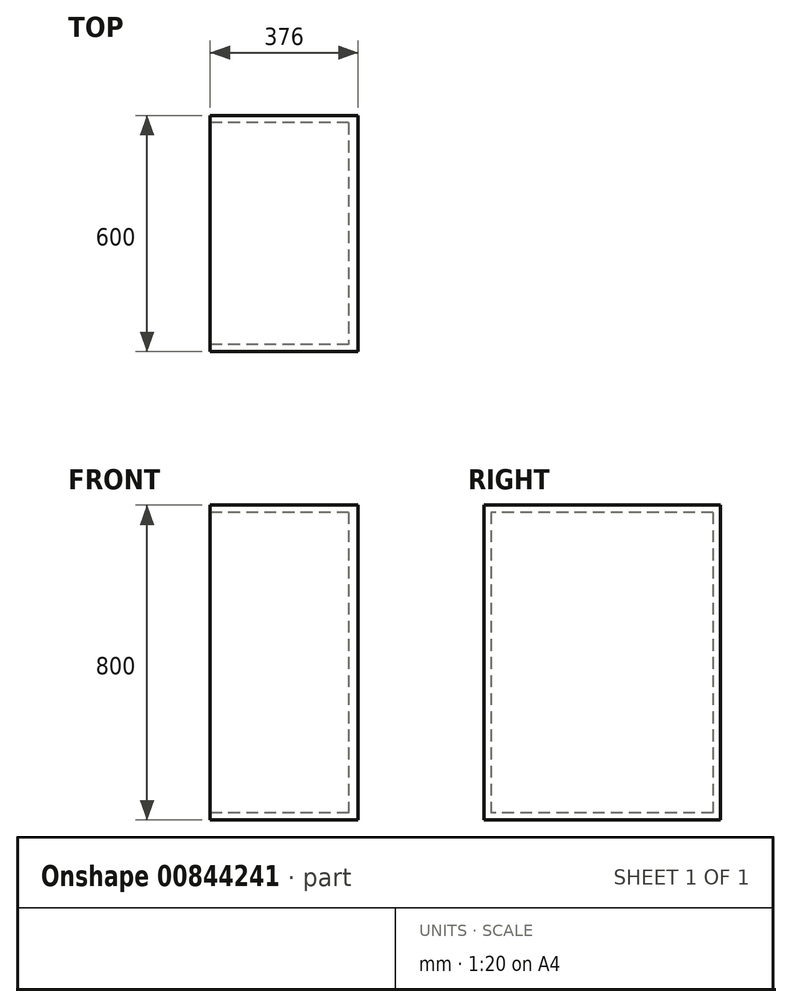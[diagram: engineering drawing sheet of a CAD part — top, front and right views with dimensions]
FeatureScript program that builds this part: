
annotation { "Feature Type Name" : "Feature", "Feature Type Description" : "" }
export const myFeature = defineFeature(function(context is Context, id is Id, definition is map)
    precondition{}
    {
        {
            var Q0;
            Q0=qCreatedBy(makeId("Top.planeOp"),FACE);
            var sketch = newSketch(context, id + "F0", { "sketchPlane" : qUnion([Q0])});
            skLineSegment(sketch, "E0.bottom", {"start": v(0, 0) * mm, "end": v(-35.12, 0) * mm});
            skLineSegment(sketch, "E0.top", {"start": v(0, -34.86) * mm, "end": v(-35.12, -34.86) * mm});
            skLineSegment(sketch, "E0.left", {"start": v(0, 0) * mm, "end": v(0, -34.86) * mm});
            skLineSegment(sketch, "E0.right", {"start": v(-35.12, 0) * mm, "end": v(-35.12, -34.86) * mm});
            skSolve(sketch);
        }
        {
            var Q0;
            Q0=makeQuery(id+"F0.imprint","IMPRINT",FACE,{"disambiguationData":[TD([[makeQuery(id+"F0.imprint","IMPRINT",EDGE,{"derivedFrom":sQuery(id+"F0.wireOp",EDGE,"E0.bottom")}),1.0]])]});
            extrude(context, id + "F1", {"entities" : qUnion([Q0]), "depth" : 800 * mm, "offsetDistance" : 25 * mm});
        }
        {
            var Q0;
            Q0=makeQuery(id+"F1.opExtrude","SWEPT_FACE",FACE,{"disambiguationData":[OSD([sQuery(id+"F0.wireOp",EDGE,"E0.bottom")])]});
            extrude(context, id + "F2", {"entities" : qUnion([Q0]), "operationType" : NewBodyOperationType.ADD, "oppositeDirection" : true, "depth" : 600 * mm, "offsetDistance" : 25 * mm});
        }
        {
            var Q0;
            {var subQ0=sQuery(id+"F0.wireOp",EDGE,"E0.left");Q0=makeQuery(id+"F2.boolean.opBoolean","MERGE",FACE,{"derivedFrom":[makeQuery(id+"F1.opExtrude","SWEPT_FACE",FACE,{"disambiguationData":[OSD([subQ0])]}),makeQuery(id+"F2.opExtrude","SWEPT_FACE",FACE,{"disambiguationData":[OSD([sQuery(id+"F0.wireOp",EDGE,"E0.bottom"),subQ0])]})]});}
            extrude(context, id + "F3", {"entities" : qUnion([Q0]), "operationType" : NewBodyOperationType.ADD, "oppositeDirection" : true, "depth" : 370 * mm, "offsetDistance" : 25 * mm});
        }
        {
            var Q0;
            Q0=makeQuery(id+"F3.opExtrude","CAP_FACE",FACE,{"disambiguationData":[OSD([sQuery(id+"F0.wireOp",EDGE,"E0.bottom"),sQuery(id+"F0.wireOp",EDGE,"E0.left")])],"isStart":false});
            shell(context, id + "F4", {"entities" : qUnion([Q0]), "thickness" : 18 * mm});
        }
        {
            var Q0;
            {var subQ0=sQuery(id+"F0.wireOp",EDGE,"E0.left");Q0=makeQuery(id+"F2.boolean.opBoolean","MERGE",FACE,{"derivedFrom":[makeQuery(id+"F1.opExtrude","SWEPT_FACE",FACE,{"disambiguationData":[OSD([subQ0])]}),makeQuery(id+"F2.opExtrude","SWEPT_FACE",FACE,{"disambiguationData":[OSD([sQuery(id+"F0.wireOp",EDGE,"E0.bottom"),subQ0])]})]});}
            extrude(context, id + "F5", {"entities" : qUnion([Q0]), "operationType" : NewBodyOperationType.ADD, "depth" : 6 * mm, "offsetDistance" : 25 * mm});
        }
    });
